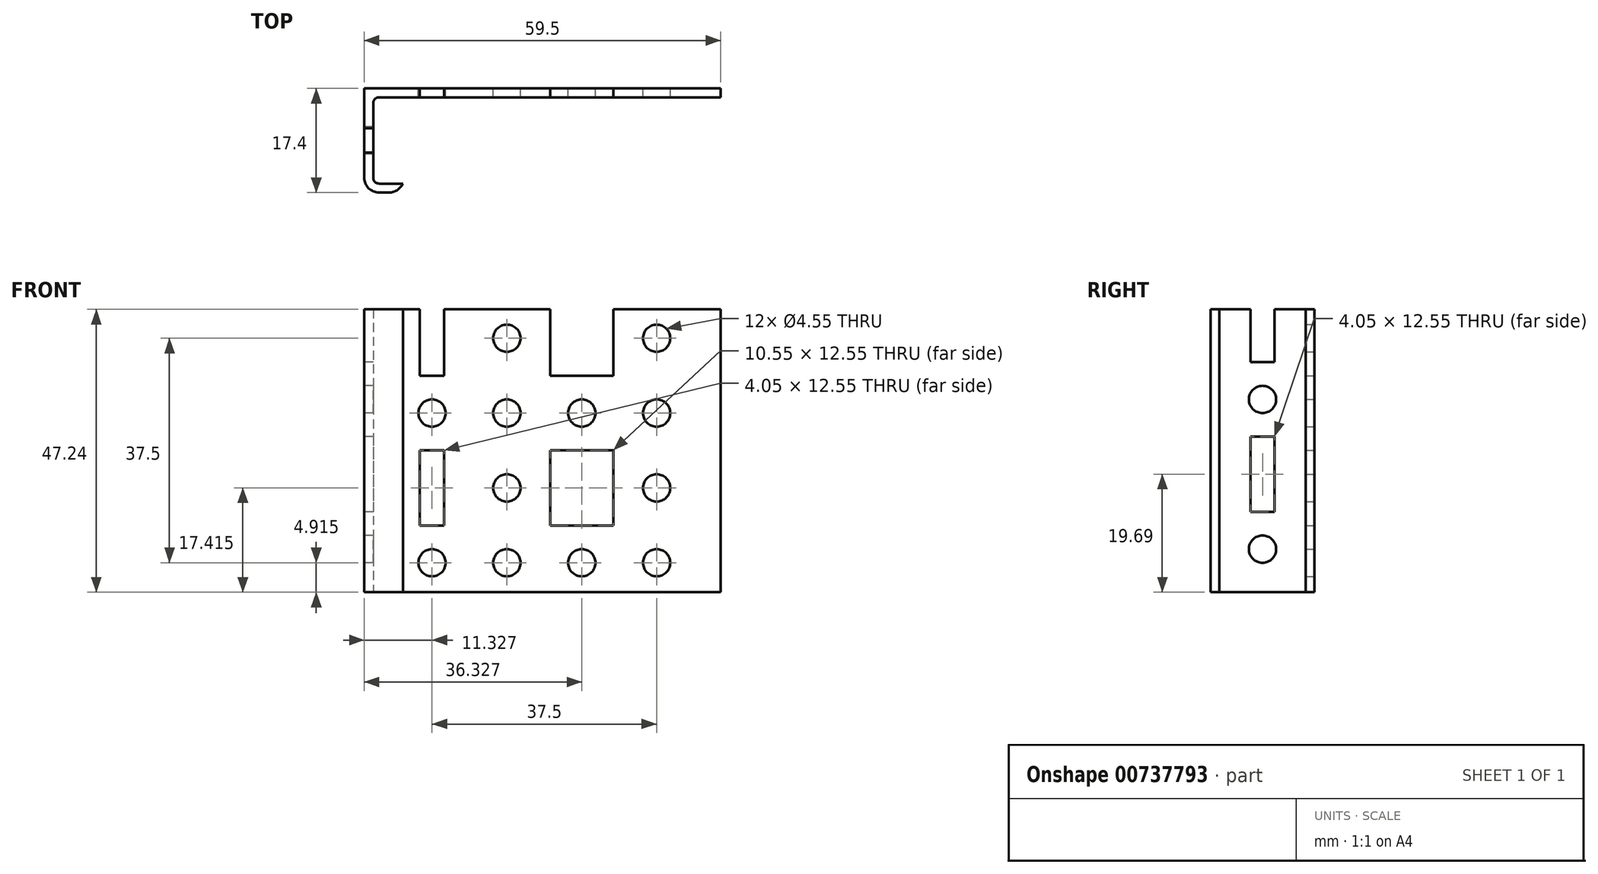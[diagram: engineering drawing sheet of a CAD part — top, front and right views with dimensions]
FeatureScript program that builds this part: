
annotation { "Feature Type Name" : "Feature", "Feature Type Description" : "" }
export const myFeature = defineFeature(function(context is Context, id is Id, definition is map)
    precondition{}
    {
        {
            var Q0;
            Q0=qCreatedBy(makeId("Top.planeOp"),FACE);
            var sketch = newSketch(context, id + "F0", { "sketchPlane" : qUnion([Q0])});
            skLineSegment(sketch, "E0.bottom", {"start": v(-2.66, 20.18) * mm, "end": v(56.84, 20.18) * mm});
            skLineSegment(sketch, "E0.top", {"start": v(-2.66, 18.68) * mm, "end": v(56.84, 18.68) * mm});
            skLineSegment(sketch, "E0.left", {"start": v(-2.66, 20.18) * mm, "end": v(-2.66, 18.68) * mm});
            skLineSegment(sketch, "E0.right", {"start": v(56.84, 20.18) * mm, "end": v(56.84, 18.68) * mm});
            skLineSegment(sketch, "E1.bottom", {"start": v(-2.66, 20.18) * mm, "end": v(-1.16, 20.18) * mm});
            skLineSegment(sketch, "E1.top", {"start": v(-2.66, 2.78) * mm, "end": v(-1.16, 2.78) * mm});
            skLineSegment(sketch, "E1.left", {"start": v(-2.66, 20.18) * mm, "end": v(-2.66, 2.78) * mm});
            skLineSegment(sketch, "E1.right", {"start": v(-1.16, 20.18) * mm, "end": v(-1.16, 2.78) * mm});
            skLineSegment(sketch, "E2.bottom", {"start": v(-2.66, 2.78) * mm, "end": v(3.8, 2.78) * mm});
            skLineSegment(sketch, "E2.top", {"start": v(-2.66, 4.28) * mm, "end": v(3.8, 4.28) * mm});
            skLineSegment(sketch, "E2.left", {"start": v(-2.66, 2.78) * mm, "end": v(-2.66, 4.28) * mm});
            skLineSegment(sketch, "E2.right", {"start": v(3.8, 2.78) * mm, "end": v(3.8, 4.28) * mm});
            skSolve(sketch);
        }
        {
            var Q0;
            Q0 = qSketchRegion(id + "F0", true);
            extrude(context, id + "F1", {"entities" : qUnion([Q0]), "depth" : 47.24 * mm, "offsetDistance" : 25 * mm});
        }
        {
            var Q0;
            Q0=makeQuery(id+"F1.opExtrude","SWEPT_EDGE",EDGE,{"disambiguationData":[OSD([sQuery(id+"F0.wireOp",EDGE,"E1.bottom"),sQuery(id+"F0.wireOp",EDGE,"E1.left")])]});
            var Q1;
            Q1=makeQuery(id+"F1.opExtrude","SWEPT_EDGE",EDGE,{"disambiguationData":[OSD([sQuery(id+"F0.wireOp",EDGE,"E2.bottom"),sQuery(id+"F0.wireOp",EDGE,"E2.left")])]});
            fillet(context, id + "F2", {"entities" : qUnion([Q0, Q1]), "radius" : 2.5 * mm, "tangentPropagation" : true, "allowEdgeOverflow" : false});
        }
        {
            var Q0;
            Q0=makeQuery(id+"F1.opExtrude","SWEPT_EDGE",EDGE,{"disambiguationData":[OSD([sQuery(id+"F0.wireOp",EDGE,"E1.right"),sQuery(id+"F0.wireOp",EDGE,"E2.top")])]});
            var Q1;
            Q1=makeQuery(id+"F1.opExtrude","SWEPT_EDGE",EDGE,{"disambiguationData":[OSD([sQuery(id+"F0.wireOp",EDGE,"E0.top"),sQuery(id+"F0.wireOp",EDGE,"E1.right")])]});
            fillet(context, id + "F3", {"entities" : qUnion([Q0, Q1]), "radius" : 1 * mm, "tangentPropagation" : true, "allowEdgeOverflow" : false});
        }
        {
            var Q0;
            Q0=makeQuery(id+"F1.opExtrude","SWEPT_FACE",FACE,{"disambiguationData":[OSD([sQuery(id+"F0.wireOp",EDGE,"E0.bottom"),sQuery(id+"F0.wireOp",EDGE,"E1.bottom")])]});
            var sketch = newSketch(context, id + "F4", { "sketchPlane" : qUnion([Q0])});
            skCircle(sketch, "E3", {"center": v(-46.17, 42.42) * mm, "radius": 2.27 * mm});
            skCircle(sketch, "E4", {"center": v(-21.17, 42.42) * mm, "radius": 2.27 * mm});
            skCircle(sketch, "E5.0.1.0", {"center": v(-21.17, 29.92) * mm, "radius": 2.27 * mm});
            skCircle(sketch, "E5.0.1.1", {"center": v(-46.17, 29.92) * mm, "radius": 2.27 * mm});
            skCircle(sketch, "E5.0.2.0", {"center": v(-21.17, 17.42) * mm, "radius": 2.27 * mm});
            skCircle(sketch, "E5.0.2.1", {"center": v(-46.17, 17.42) * mm, "radius": 2.27 * mm});
            skCircle(sketch, "E5.0.3.0", {"center": v(-21.17, 4.92) * mm, "radius": 2.27 * mm});
            skCircle(sketch, "E5.0.3.1", {"center": v(-46.17, 4.92) * mm, "radius": 2.27 * mm});
            skLineSegment(sketch, "E5.direction1", {"start": v(-46.17, 42.42) * mm, "end": v(-21.17, 42.42) * mm, "construction": true});
            skLineSegment(sketch, "E5.direction2", {"start": v(-46.17, 42.42) * mm, "end": v(-46.17, 29.92) * mm, "construction": true});
            skCircle(sketch, "E6", {"center": v(-33.67, 29.92) * mm, "radius": 2.27 * mm});
            skCircle(sketch, "E7.0.1.0", {"center": v(-33.67, 4.92) * mm, "radius": 2.27 * mm});
            skCircle(sketch, "E7.1.0.0", {"center": v(-8.67, 29.92) * mm, "radius": 2.27 * mm});
            skCircle(sketch, "E7.1.1.0", {"center": v(-8.67, 4.92) * mm, "radius": 2.27 * mm});
            skLineSegment(sketch, "E7.direction1", {"start": v(-33.67, 29.92) * mm, "end": v(-8.67, 29.92) * mm, "construction": true});
            skLineSegment(sketch, "E7.direction2", {"start": v(-33.67, 29.92) * mm, "end": v(-33.67, 4.92) * mm, "construction": true});
            skLineSegment(sketch, "E8.bottom", {"start": v(-28.4, 11.14) * mm, "end": v(-38.94, 11.14) * mm});
            skLineSegment(sketch, "E8.top", {"start": v(-28.4, 23.7) * mm, "end": v(-38.94, 23.7) * mm});
            skLineSegment(sketch, "E8.left", {"start": v(-28.4, 11.14) * mm, "end": v(-28.4, 23.7) * mm});
            skLineSegment(sketch, "E8.right", {"start": v(-38.94, 11.14) * mm, "end": v(-38.94, 23.7) * mm});
            skPoint(sketch, "E8.middle", {"position": v(-33.67, 17.42) * mm});
            skLineSegment(sketch, "E9.0.1.0", {"start": v(-38.94, 36.14) * mm, "end": v(-38.94, 48.7) * mm});
            skLineSegment(sketch, "E9.0.1.1", {"start": v(-28.4, 48.7) * mm, "end": v(-38.94, 48.7) * mm});
            skPoint(sketch, "E9.0.1.2", {"position": v(-33.67, 42.42) * mm});
            skLineSegment(sketch, "E9.0.1.3", {"start": v(-28.4, 36.14) * mm, "end": v(-38.94, 36.14) * mm});
            skLineSegment(sketch, "E9.0.1.4", {"start": v(-28.4, 36.14) * mm, "end": v(-28.4, 48.7) * mm});
            skLineSegment(sketch, "E9.direction1", {"start": v(-38.94, 11.14) * mm, "end": v(-13.94, 11.14) * mm, "construction": true});
            skLineSegment(sketch, "E9.direction2", {"start": v(-38.94, 11.14) * mm, "end": v(-38.94, 36.14) * mm, "construction": true});
            skLineSegment(sketch, "E10.bottom", {"start": v(-6.64, 11.14) * mm, "end": v(-10.7, 11.14) * mm});
            skLineSegment(sketch, "E10.top", {"start": v(-6.64, 23.7) * mm, "end": v(-10.7, 23.7) * mm});
            skLineSegment(sketch, "E10.left", {"start": v(-6.64, 11.14) * mm, "end": v(-6.64, 23.7) * mm});
            skLineSegment(sketch, "E10.right", {"start": v(-10.7, 11.14) * mm, "end": v(-10.7, 23.7) * mm});
            skPoint(sketch, "E10.middle", {"position": v(-8.67, 17.42) * mm});
            skLineSegment(sketch, "E11.0.1.0", {"start": v(-6.64, 48.7) * mm, "end": v(-10.7, 48.7) * mm});
            skLineSegment(sketch, "E11.0.1.1", {"start": v(-6.64, 36.14) * mm, "end": v(-10.7, 36.14) * mm});
            skPoint(sketch, "E11.0.1.2", {"position": v(-8.67, 42.42) * mm});
            skLineSegment(sketch, "E11.0.1.3", {"start": v(-6.64, 36.14) * mm, "end": v(-6.64, 48.7) * mm});
            skLineSegment(sketch, "E11.0.1.4", {"start": v(-10.7, 36.14) * mm, "end": v(-10.7, 48.7) * mm});
            skLineSegment(sketch, "E11.direction1", {"start": v(-10.7, 11.14) * mm, "end": v(14.3, 11.14) * mm, "construction": true});
            skLineSegment(sketch, "E11.direction2", {"start": v(-10.7, 11.14) * mm, "end": v(-10.7, 36.14) * mm, "construction": true});
            skSolve(sketch);
        }
        {
            var Q0;
            Q0 = qSketchRegion(id + "F4", true);
            extrude(context, id + "F5", {"entities" : qUnion([Q0]), "operationType" : NewBodyOperationType.REMOVE, "endBound" : BoundingType.THROUGH_ALL, "oppositeDirection" : true, "depth" : 25 * mm, "offsetDistance" : 25 * mm});
        }
        {
            var Q0;
            Q0=makeQuery(id+"F1.opExtrude","SWEPT_FACE",FACE,{"disambiguationData":[OSD([sQuery(id+"F0.wireOp",EDGE,"E1.left"),sQuery(id+"F0.wireOp",EDGE,"E2.left")])]});
            var sketch = newSketch(context, id + "F6", { "sketchPlane" : qUnion([Q0])});
            skCircle(sketch, "E12", {"center": v(-11.48, 32.2) * mm, "radius": 2.27 * mm});
            skPoint(sketch, "E12.centerSnap0", {"position": v(-11.48, 47.24) * mm});
            skCircle(sketch, "E13", {"center": v(-11.48, 7.2) * mm, "radius": 2.27 * mm});
            skLineSegment(sketch, "E14.bottom", {"start": v(-9.46, 13.42) * mm, "end": v(-13.5, 13.42) * mm});
            skLineSegment(sketch, "E14.top", {"start": v(-9.46, 25.97) * mm, "end": v(-13.5, 25.97) * mm});
            skLineSegment(sketch, "E14.left", {"start": v(-9.46, 13.42) * mm, "end": v(-9.46, 25.97) * mm});
            skLineSegment(sketch, "E14.right", {"start": v(-13.5, 13.42) * mm, "end": v(-13.5, 25.97) * mm});
            skPoint(sketch, "E14.middle", {"position": v(-11.48, 19.7) * mm});
            skLineSegment(sketch, "E15.0.1.0", {"start": v(-9.46, 38.42) * mm, "end": v(-13.5, 38.42) * mm});
            skLineSegment(sketch, "E15.0.1.1", {"start": v(-9.46, 50.97) * mm, "end": v(-13.5, 50.97) * mm});
            skLineSegment(sketch, "E15.0.1.2", {"start": v(-9.46, 38.42) * mm, "end": v(-9.46, 50.97) * mm});
            skLineSegment(sketch, "E15.0.1.3", {"start": v(-13.5, 38.42) * mm, "end": v(-13.5, 50.97) * mm});
            skPoint(sketch, "E15.0.1.4", {"position": v(-11.48, 44.7) * mm});
            skLineSegment(sketch, "E15.direction1", {"start": v(-13.5, 13.42) * mm, "end": v(11.5, 13.42) * mm, "construction": true});
            skLineSegment(sketch, "E15.direction2", {"start": v(-13.5, 13.42) * mm, "end": v(-13.5, 38.42) * mm, "construction": true});
            skSolve(sketch);
        }
        {
            var Q0;
            {var subQ0=sQuery(id+"F6.wireOp",EDGE,"E15.0.1.0");Q0=makeQuery(id+"F6.imprint","IMPRINT",FACE,{"disambiguationData":[TD([[makeQuery(id+"F6.imprint","IMPRINT",EDGE,{"derivedFrom":subQ0}),-1.0]])]});}
            var Q1;
            Q1=makeQuery(id+"F6.imprint","IMPRINT",FACE,{"disambiguationData":[TD([[makeQuery(id+"F6.imprint","IMPRINT",EDGE,{"derivedFrom":sQuery(id+"F6.wireOp",EDGE,"E12")}),1.0]])]});
            var Q2;
            Q2=makeQuery(id+"F6.imprint","IMPRINT",FACE,{"disambiguationData":[TD([[makeQuery(id+"F6.imprint","IMPRINT",EDGE,{"derivedFrom":sQuery(id+"F6.wireOp",EDGE,"E14.bottom")}),-1.0]])]});
            var Q3;
            Q3=makeQuery(id+"F6.imprint","IMPRINT",FACE,{"disambiguationData":[TD([[makeQuery(id+"F6.imprint","IMPRINT",EDGE,{"derivedFrom":sQuery(id+"F6.wireOp",EDGE,"E13")}),1.0]])]});
            extrude(context, id + "F7", {"entities" : qUnion([Q0, Q1, Q2, Q3]), "operationType" : NewBodyOperationType.REMOVE, "oppositeDirection" : true, "depth" : 25 * mm, "offsetDistance" : 25 * mm});
        }
    });
